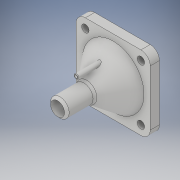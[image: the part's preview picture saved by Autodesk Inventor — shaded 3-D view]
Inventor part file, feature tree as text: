
AUTODESK INVENTOR PART (.ipt)
format: ipt  version: 2018 (Build 220112000, 112)  size: 365,568 bytes
history: native  units: in
note: dims shown in document units (in); Inventor stores cm internally (conversion verified against a paired STEP export)
features: extrude x12, sketch x10, fillet x4, projected_geometry x3, chamfer x2, hole x2, plane x1, loft x1, shell x1, pattern_circular x1
ambient origin geometry x8: Origin, YZ Plane, XZ Plane, XY Plane, X Axis, Y Axis, Z Axis, Center Point
bodies: Body1 (feature_tree)
feature tree (37):
  sketch  "Sketch26"  dims[d127=2.0in d128=4.0in d129=3.325in]
  plane  "Work Plane3"
  loft  "Loft2"
  shell  "Shell2"  Thickness=3.325in
  extrude  "Extrusion31"  Depth=1.0in
  fillet  "Fillet5"  [1 undecoded]
  extrude  "Extrusion32"  Depth=0.15in
  sketch  "Sketch31"  dims[d144=0.75in d145=0.5in d146=0.0in]
  extrude  "Extrusion33"  Depth=0.5in
  extrude  "Extrusion34"  Depth=0.5in TaperAngle=0.0deg
  extrude  "Extrusion35"  Depth=0.625in
  fillet  "Fillet6"  Radius=0.505in
  pattern_circular  "Circular Pattern4"  [2 undecoded]
  extrude  "Extrusion36"  Depth=0.5in TaperAngle=360.0deg
  fillet  "Fillet7"  Radius=1.5in
  chamfer  "Chamfer5"  Distance=0.25in
  sketch  "Sketch33"  dims[d150=0.25in]
  extrude  "Extrusion37"  Depth=0.125in TaperAngle=45.0deg
  extrude  "Extrusion38"  Depth=0.5in
  extrude  "Extrusion39"  Depth=0.25in
  chamfer  "Chamfer6"  Distance=0.05in
  extrude  "Extrusion40"  Depth=0.5in TaperAngle=0.0deg
  hole  "Hole2"  [1 undecoded]
  extrude  "Extrusion41"  Depth=0.5in TaperAngle=0.0deg
  extrude  "Extrusion42"  Depth=0.125in TaperAngle=45.0deg
  fillet  "Fillet8"  Radius=0.5in
  sketch  "Sketch27"  dims[d130=1.5in d131=1.0in d136=0.0in d137=90.0deg]
  sketch  "Sketch28"  dims[d138=0.0in d139=90.0deg d140=0.15in]
  projected_geometry  "Projected Loop14"
  sketch  "Sketch29"  dims[d141=0.5in d142=0.0in d143=1.0in]
  projected_geometry  "Projected Loop15"
  sketch  "Sketch32"  dims[d147=1.0in d148=0.625in d149=0.505in]
  sketch  "Sketch34"  dims[d151=0.5in d152=0.0in]
  hole  "Hole1"  [1 undecoded]
  sketch  "Sketch35"  dims[d153=0.5in d154=0.0in]
  sketch  "Sketch36"  dims[d155=0.2in d156=0.0in d157=0.25in d158=0.7874in d159=360.0deg d161=1.5in d162=0.0in d163=0.25in d164=0.125in d165=0.125in d166=45.0deg d167=1.0in d168=0.25in d169=0.05in d170=1.5in d171=0.0in d172=1.5in d173=0.0in d174=0.5in d175=0.0in d176=0.025in d177=0.125in d178=45.0deg d179=0.5in d180=0.0in d181=0.397in d182=0.75in d183=0.375in d184=0.25in d185=0.5635in d186=1.0in d187=0.0in d188=0.5in d189=0.0in d190=0.5in d191=0.0in d192=0.5in]
  projected_geometry  "Projected Loop16"
note: 5 required parameter values undecoded (feature->parameter linkage not recoverable at this tier; creation-order binding heuristic only, values carry confidence <= 0.55)
